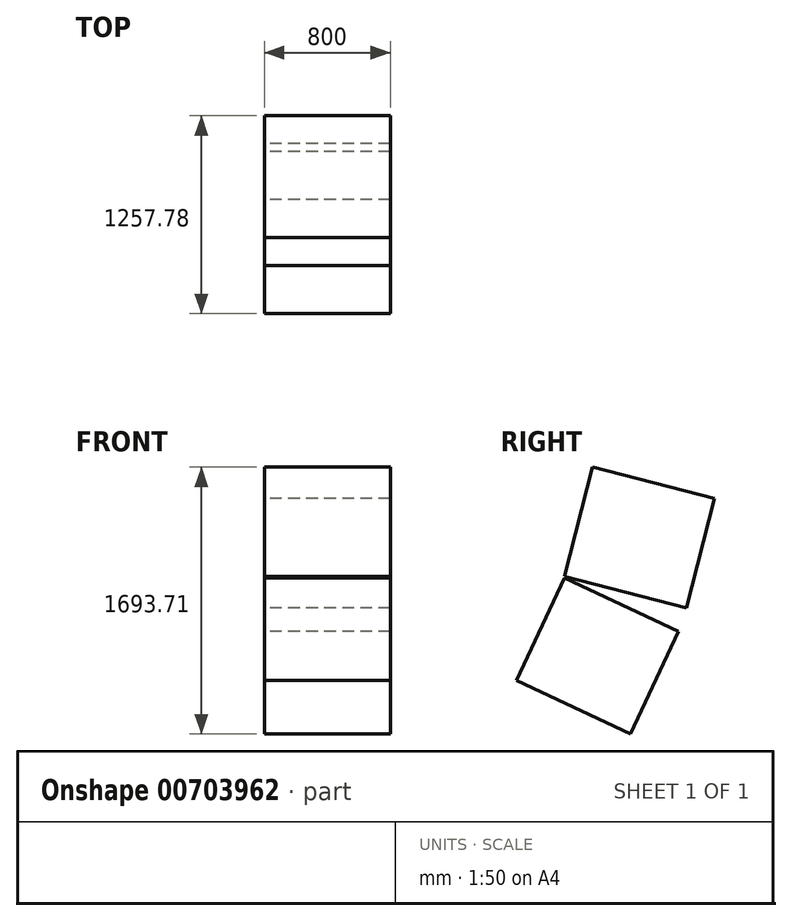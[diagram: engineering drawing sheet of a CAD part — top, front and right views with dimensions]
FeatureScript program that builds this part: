
annotation { "Feature Type Name" : "Feature", "Feature Type Description" : "" }
export const myFeature = defineFeature(function(context is Context, id is Id, definition is map)
    precondition{}
    {
        {
            var Q0;
            Q0=qCreatedBy(makeId("Right.planeOp"),FACE);
            var sketch = newSketch(context, id + "F0", { "sketchPlane" : qUnion([Q0])});
            skLineSegment(sketch, "E0", {"start": v(0, 0) * mm, "end": v(1919, 0) * mm});
            skLineSegment(sketch, "E1", {"start": v(0, 0) * mm, "end": v(-3081, 0) * mm});
            skLineSegment(sketch, "E2", {"start": v(1919, 0) * mm, "end": v(2925.5, 1199.51) * mm});
            skLineSegment(sketch, "E3", {"start": v(-3081, 1199.51) * mm, "end": v(-3081, 0) * mm});
            skLineSegment(sketch, "E4", {"start": v(20313, -8599) * mm, "end": v(4857, -10124) * mm});
            skLineSegment(sketch, "E5", {"start": v(4857, -10124) * mm, "end": v(1919, -10124) * mm});
            skLineSegment(sketch, "E6", {"start": v(1919, -10124) * mm, "end": v(1919, -9142) * mm});
            skLineSegment(sketch, "E7", {"start": v(1919, -9142) * mm, "end": v(-3081, -9142) * mm});
            skLineSegment(sketch, "E8", {"start": v(4857, -10124) * mm, "end": v(20313, -10124) * mm, "construction": true});
            skLineSegment(sketch, "E9", {"start": v(20313, -10124) * mm, "end": v(20313, -8599) * mm, "construction": true});
            skLineSegment(sketch, "E10", {"start": v(20313, -8599) * mm, "end": v(20313, 415.28) * mm});
            skLineSegment(sketch, "E11", {"start": v(20313, 415.28) * mm, "end": v(20785.63, 415.28) * mm});
            skSolve(sketch);
        }
        {
            var Q0;
            Q0=qCreatedBy(makeId("Right.planeOp"),FACE);
            var sketch = newSketch(context, id + "F1", { "sketchPlane" : qUnion([Q0])});
            skLineSegment(sketch, "E12.bottom", {"start": v(-400, -4003) * mm, "end": v(374.98, -4201.5) * mm});
            skLineSegment(sketch, "E12.top", {"start": v(-577.9, -4697.58) * mm, "end": v(197.07, -4896.08) * mm});
            skLineSegment(sketch, "E12.left", {"start": v(-400, -4003) * mm, "end": v(-577.9, -4697.58) * mm});
            skLineSegment(sketch, "E12.right", {"start": v(374.98, -4201.5) * mm, "end": v(197.07, -4896.08) * mm});
            skLineSegment(sketch, "E13.bottom", {"start": v(-577.9, -4707.58) * mm, "end": v(146.16, -5047.76) * mm});
            skLineSegment(sketch, "E13.top", {"start": v(-882.8, -5356.52) * mm, "end": v(-158.74, -5696.7) * mm});
            skLineSegment(sketch, "E13.left", {"start": v(-577.9, -4707.58) * mm, "end": v(-882.8, -5356.52) * mm});
            skLineSegment(sketch, "E13.right", {"start": v(146.16, -5047.76) * mm, "end": v(-158.74, -5696.7) * mm});
            skLineSegment(sketch, "E14", {"start": v(197.07, -4896.08) * mm, "end": v(146.16, -5047.76) * mm, "construction": true});
            skLineSegment(sketch, "E15", {"start": v(-577.9, -4697.58) * mm, "end": v(-577.9, -4707.58) * mm, "construction": true});
            skLineSegment(sketch, "E16", {"start": v(286.03, -4548.8) * mm, "end": v(17270.46, -8899.2) * mm, "construction": true});
            skLineSegment(sketch, "E17", {"start": v(-6.29, -5372.24) * mm, "end": v(9196.26, -9695.86) * mm, "construction": true});
            skLineSegment(sketch, "E18", {"start": v(-6.29, -5372.24) * mm, "end": v(18814.24, -8746.88) * mm});
            skLineSegment(sketch, "E19", {"start": v(-6.29, -5372.24) * mm, "end": v(5543.31, -10056.28) * mm});
            skLineSegment(sketch, "E20", {"start": v(0, 0) * mm, "end": v(0, -3993) * mm, "construction": true});
            skLineSegment(sketch, "E21", {"start": v(-400, -3993) * mm, "end": v(400, -3993) * mm});
            skLineSegment(sketch, "E22", {"start": v(400, -3993) * mm, "end": v(374.98, -4201.5) * mm, "construction": true});
            skLineSegment(sketch, "E23", {"start": v(-400, -3993) * mm, "end": v(-400, -4003) * mm, "construction": true});
            skLineSegment(sketch, "E24", {"start": v(18814.24, -8746.88) * mm, "end": v(5543.31, -10056.28) * mm});
            skLineSegment(sketch, "E25", {"start": v(286.03, -4548.8) * mm, "end": v(9397.63, -9675.99) * mm});
            skLineSegment(sketch, "E26", {"start": v(286.03, -4548.8) * mm, "end": v(69064.9, -3788.79) * mm});
            skLineSegment(sketch, "E27", {"start": v(69064.9, -3788.79) * mm, "end": v(9397.63, -9675.99) * mm});
            skSolve(sketch);
        }
        {
            var Q0;
            Q0=makeQuery(id+"F1.imprint","IMPRINT",FACE,{"disambiguationData":[TD([[makeQuery(id+"F1.imprint","IMPRINT",EDGE,{"derivedFrom":sQuery(id+"F1.wireOp",EDGE,"E12.bottom")}),-1.0]])]});
            var Q1;
            Q1=makeQuery(id+"F1.imprint","IMPRINT",FACE,{"disambiguationData":[TD([[makeQuery(id+"F1.imprint","IMPRINT",EDGE,{"derivedFrom":sQuery(id+"F1.wireOp",EDGE,"E13.bottom")}),-1.0]])]});
            extrude(context, id + "F2", {"entities" : qUnion([Q0, Q1]), "endBound" : BoundingType.SYMMETRIC, "depth" : 800 * mm, "offsetDistance" : 25 * mm});
        }
        {
            var Q0;
            Q0=sQuery(id+"F0.wireOp",EDGE,"E1");
            var Q1;
            Q1=sQuery(id+"F0.wireOp",EDGE,"E0");
            var Q2;
            Q2=sQuery(id+"F0.wireOp",EDGE,"E2");
            var Q3;
            Q3=sQuery(id+"F0.wireOp",EDGE,"E3");
            var Q4;
            Q4=sQuery(id+"F0.wireOp",EDGE,"E7");
            var Q5;
            Q5=sQuery(id+"F0.wireOp",EDGE,"E6");
            var Q6;
            Q6=sQuery(id+"F0.wireOp",EDGE,"E5");
            var Q7;
            Q7=sQuery(id+"F0.wireOp",EDGE,"E4");
            var Q8;
            Q8=sQuery(id+"F0.wireOp",EDGE,"E10");
            var Q9;
            Q9=sQuery(id+"F0.wireOp",EDGE,"E11");
            extrude(context, id + "F3", {"bodyType" : ToolBodyType.SURFACE, "surfaceEntities" : qUnion([Q0, Q1, Q2, Q3, Q4, Q5, Q6, Q7, Q8, Q9]), "endBound" : BoundingType.SYMMETRIC, "depth" : 12000 * mm, "offsetDistance" : 25 * mm});
        }
        {
            var Q0;
            Q0=makeQuery(id+"F2.opExtrude","CAP_EDGE",EDGE,{"disambiguationData":[OSD([sQuery(id+"F1.wireOp",EDGE,"E12.right")])],"isStart":false});
            cPoint(context, id + "F4", {"entities" : qUnion([Q0]), "parameter" : 0.5});
        }
        {
            var Q0;
            Q0=sQuery(id+"F1.wireOp",VERTEX,"E25.start");
            var Q1;
            Q1 = qCreatedBy(id + "F4" ,VERTEX);
            var Q2;
            Q2=sQuery(id+"F1.wireOp",VERTEX,"E16.end");
            cPlane(context, id + "F5", {"entities" : qUnion([Q0, Q1, Q2]), "cplaneType" : CPlaneType.THREE_POINT, "offset" : 25 * mm, "width" : 150 * mm, "height" : 150 * mm});
        }
        {
            var Q0;
            Q0=makeQuery(id+"F2.opExtrude","CAP_EDGE",EDGE,{"disambiguationData":[OSD([sQuery(id+"F1.wireOp",EDGE,"E13.right")])],"isStart":false});
            cPoint(context, id + "F6", {"entities" : qUnion([Q0]), "parameter" : 0.5});
        }
        {
            var Q0;
            Q0=sQuery(id+"F1.wireOp",VERTEX,"E18.start");
            var Q1;
            Q1 = qCreatedBy(id + "F6" ,VERTEX);
            var Q2;
            Q2=sQuery(id+"F1.wireOp",VERTEX,"E17.end");
            cPlane(context, id + "F7", {"entities" : qUnion([Q0, Q1, Q2]), "cplaneType" : CPlaneType.THREE_POINT, "offset" : 25 * mm, "width" : 150 * mm, "height" : 150 * mm});
        }
    });
